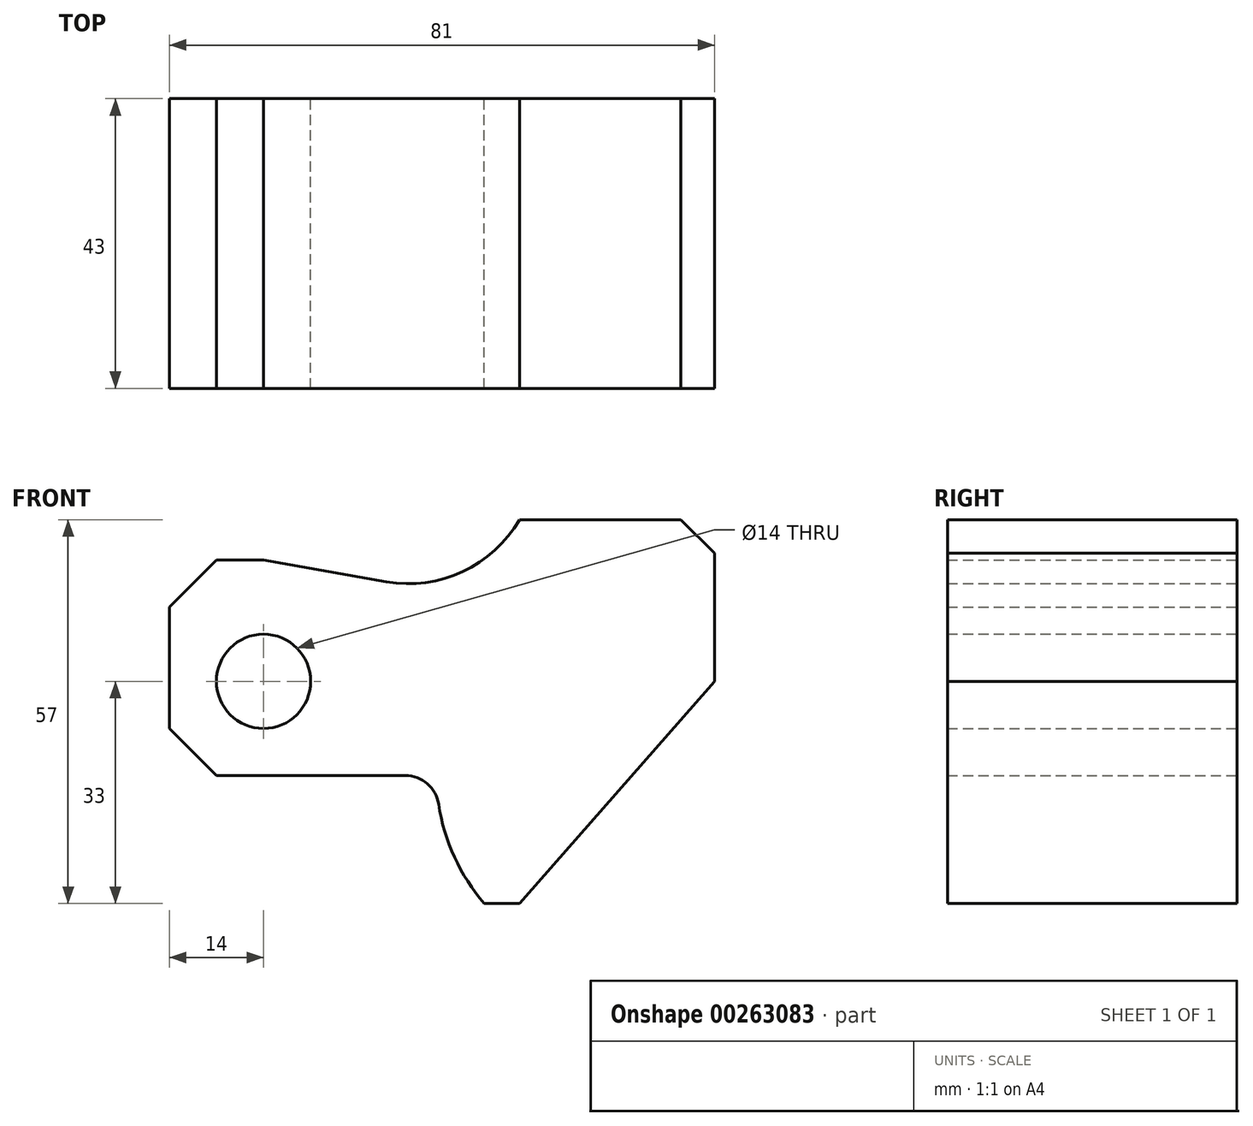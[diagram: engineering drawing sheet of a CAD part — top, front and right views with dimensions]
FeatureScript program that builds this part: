
annotation { "Feature Type Name" : "Feature", "Feature Type Description" : "" }
export const myFeature = defineFeature(function(context is Context, id is Id, definition is map)
    precondition{}
    {
        {
            var Q0;
            Q0=qCreatedBy(makeId("Front.planeOp"),FACE);
            var sketch = newSketch(context, id + "F0", { "sketchPlane" : qUnion([Q0])});
            skCircle(sketch, "E0", {"center": v(0, 0) * mm, "radius": 7 * mm});
            skLineSegment(sketch, "E1", {"start": v(-14, 11) * mm, "end": v(-14, -7) * mm});
            skLineSegment(sketch, "E2", {"start": v(-14, -7) * mm, "end": v(-7, -14) * mm});
            skLineSegment(sketch, "E3", {"start": v(67, 0) * mm, "end": v(67, 19) * mm});
            skLineSegment(sketch, "E4", {"start": v(67, 19) * mm, "end": v(62, 24) * mm});
            skLineSegment(sketch, "E5", {"start": v(62, 24) * mm, "end": v(38, 24) * mm});
            skArc(sketch, "E6", {"start": v(18.24, 14.78) * mm, "mid": v(29.57, 16.28) * mm, "end": v(38, 24) * mm});
            skLineSegment(sketch, "E7", {"start": v(18.24, 14.78) * mm, "end": v(0, 18) * mm});
            skLineSegment(sketch, "E8", {"start": v(0, 18) * mm, "end": v(-7, 18) * mm});
            skLineSegment(sketch, "E9", {"start": v(-7, 18) * mm, "end": v(-14, 11) * mm});
            skLineSegment(sketch, "E10", {"start": v(0, 18) * mm, "end": v(10.62, 18) * mm, "construction": true});
            skLineSegment(sketch, "E11", {"start": v(-7, -14) * mm, "end": v(21.07, -14) * mm});
            skLineSegment(sketch, "E12", {"start": v(38, -33) * mm, "end": v(32.79, -33) * mm});
            skLineSegment(sketch, "E13", {"start": v(38, -33) * mm, "end": v(67, 0) * mm});
            skArc(sketch, "E14", {"start": v(26.01, -18.26) * mm, "mid": v(28.35, -26.12) * mm, "end": v(32.79, -33) * mm});
            skArc(sketch, "E15", {"start": v(26.01, -18.26) * mm, "mid": v(24.33, -15.21) * mm, "end": v(21.07, -14) * mm});
            skSolve(sketch);
        }
        {
            var Q0;
            Q0 = qSketchRegion(id + "F0", true);
            extrude(context, id + "F1", {"entities" : qUnion([Q0]), "depth" : 43 * mm});
        }
    });
